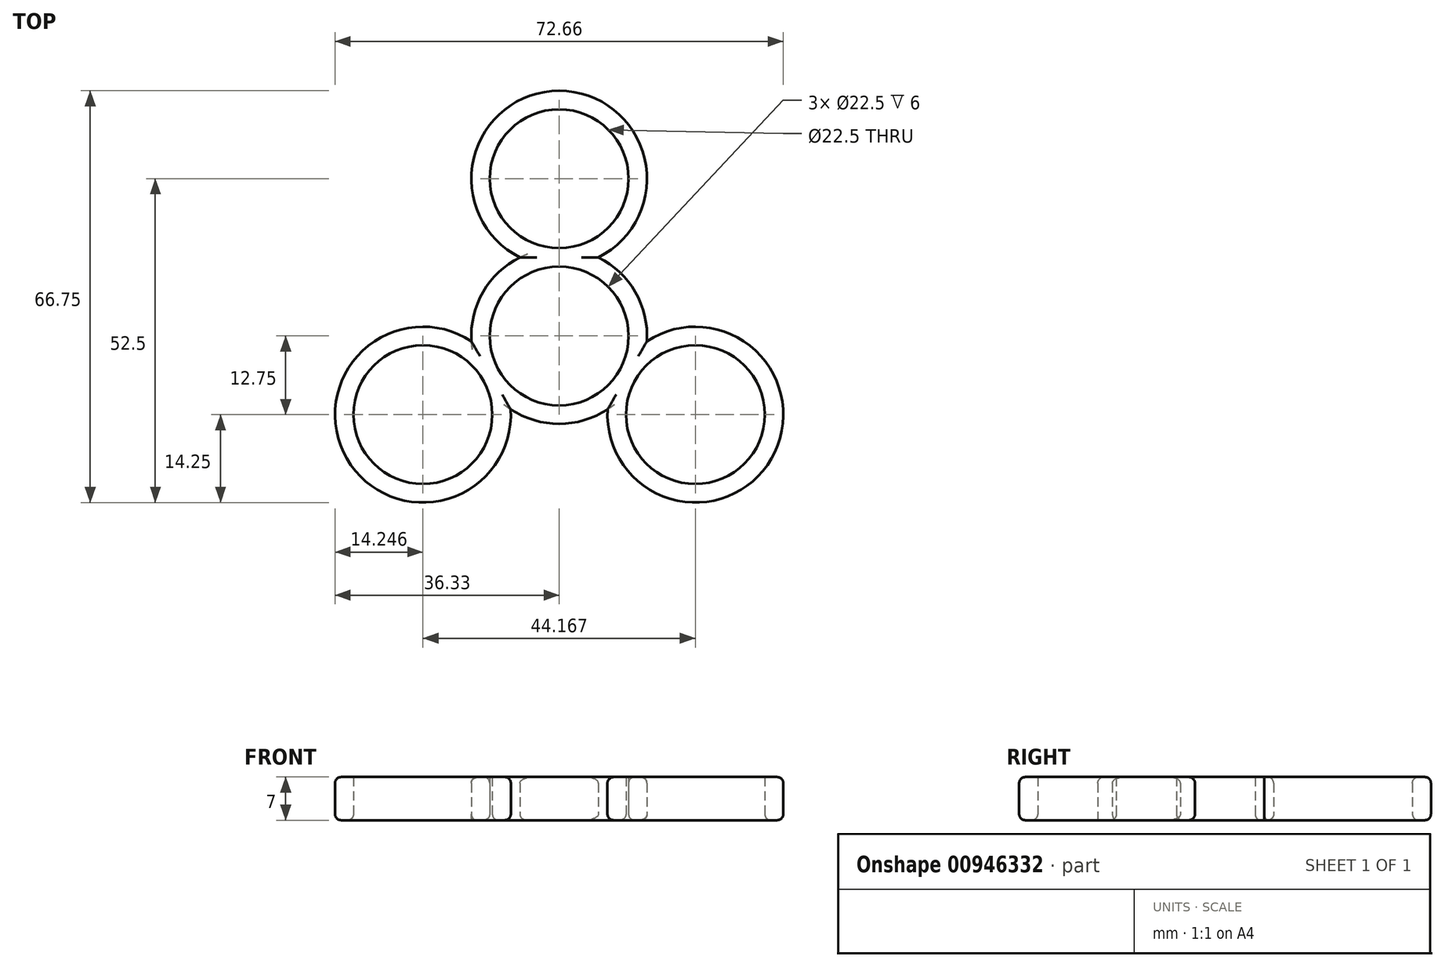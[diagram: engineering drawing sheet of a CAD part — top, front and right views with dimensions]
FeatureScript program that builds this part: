
annotation { "Feature Type Name" : "Feature", "Feature Type Description" : "" }
export const myFeature = defineFeature(function(context is Context, id is Id, definition is map)
    precondition{}
    {
        {
            var Q0;
            Q0=qCreatedBy(makeId("Top.planeOp"),FACE);
            var sketch = newSketch(context, id + "F0", { "sketchPlane" : qUnion([Q0])});
            skArc(sketch, "E0", {"start": v(9.74, 5.62) * mm, "mid": v(0, 11.25) * mm, "end": v(-9.74, 5.62) * mm});
            skCircle(sketch, "E1", {"center": v(0, 25.5) * mm, "radius": 11.25 * mm});
            skArc(sketch, "E2", {"start": v(-6.36, 12.75) * mm, "mid": v(-9.77, 10.38) * mm, "end": v(-12.34, 7.12) * mm});
            skArc(sketch, "E3", {"start": v(6.36, 12.75) * mm, "mid": v(0, 39.75) * mm, "end": v(-6.36, 12.75) * mm});
            skArc(sketch, "E4.trimOffspring", {"start": v(12.34, 7.12) * mm, "mid": v(9.77, 10.38) * mm, "end": v(6.36, 12.75) * mm});
            skArc(sketch, "E5.1.0", {"start": v(-14.22, -0.86) * mm, "mid": v(-34.42, -19.87) * mm, "end": v(-7.86, -11.89) * mm});
            skCircle(sketch, "E5.1.1", {"center": v(-22.08, -12.75) * mm, "radius": 11.25 * mm});
            skArc(sketch, "E5.1.2", {"start": v(-7.86, -11.89) * mm, "mid": v(-4.1, -13.65) * mm, "end": v(0, -14.25) * mm});
            skArc(sketch, "E5.1.3", {"start": v(-9.74, 5.63) * mm, "mid": v(-9.74, -5.62) * mm, "end": v(0, -11.25) * mm});
            skArc(sketch, "E5.1.4", {"start": v(-12.34, 7.13) * mm, "mid": v(-13.87, 3.27) * mm, "end": v(-14.22, -0.86) * mm});
            skArc(sketch, "E5.2.0", {"start": v(7.86, -11.89) * mm, "mid": v(34.42, -19.88) * mm, "end": v(14.22, -0.86) * mm});
            skCircle(sketch, "E5.2.1", {"center": v(22.08, -12.75) * mm, "radius": 11.25 * mm});
            skArc(sketch, "E5.2.2", {"start": v(14.22, -0.86) * mm, "mid": v(13.87, 3.27) * mm, "end": v(12.34, 7.12) * mm});
            skArc(sketch, "E5.2.3", {"start": v(0, -11.25) * mm, "mid": v(9.74, -5.63) * mm, "end": v(9.74, 5.62) * mm});
            skArc(sketch, "E5.2.4", {"start": v(0, -14.25) * mm, "mid": v(4.1, -13.65) * mm, "end": v(7.86, -11.89) * mm});
            skLineSegment(sketch, "E6", {"start": v(4.42, 25.5) * mm, "end": v(-4.48, 25.5) * mm});
            skLineSegment(sketch, "E7", {"start": v(0, 21.78) * mm, "end": v(0, 30.17) * mm});
            skLineSegment(sketch, "E8", {"start": v(0, 4.75) * mm, "end": v(0, -5.57) * mm});
            skLineSegment(sketch, "E9", {"start": v(3.64, 0) * mm, "end": v(-3.58, 0) * mm});
            skLineSegment(sketch, "E10", {"start": v(22.08, -8.41) * mm, "end": v(22.08, -18.09) * mm});
            skLineSegment(sketch, "E11", {"start": v(17.58, -12.75) * mm, "end": v(27.39, -12.75) * mm});
            skLineSegment(sketch, "E12", {"start": v(-22.08, -9.06) * mm, "end": v(-22.08, -17.31) * mm});
            skLineSegment(sketch, "E13", {"start": v(-26.94, -12.75) * mm, "end": v(-17, -12.75) * mm});
            skSolve(sketch);
        }
        {
            var Q0;
            Q0 = qSketchRegion(id + "F0", true);
            extrude(context, id + "F1", {"entities" : qUnion([Q0]), "depth" : 7 * mm, "offsetDistance" : 25 * mm});
        }
        {
            var Q0;
            Q0=makeQuery(id+"F1.opExtrude","CAP_EDGE",EDGE,{"disambiguationData":[OSD([sQuery(id+"F0.wireOp",EDGE,"E3")])],"isStart":false});
            var Q1;
            Q1=makeQuery(id+"F1.opExtrude","CAP_EDGE",EDGE,{"disambiguationData":[OSD([sQuery(id+"F0.wireOp",EDGE,"E5.2.0")])],"isStart":false});
            var Q2;
            Q2=makeQuery(id+"F1.opExtrude","CAP_EDGE",EDGE,{"disambiguationData":[OSD([sQuery(id+"F0.wireOp",EDGE,"E5.1.0")])],"isStart":false});
            var Q3;
            Q3=makeQuery(id+"F1.opExtrude","CAP_EDGE",EDGE,{"disambiguationData":[OSD([sQuery(id+"F0.wireOp",EDGE,"E2"),sQuery(id+"F0.wireOp",EDGE,"E5.1.4")])],"isStart":false});
            var Q4;
            Q4=makeQuery(id+"F1.opExtrude","CAP_EDGE",EDGE,{"disambiguationData":[OSD([sQuery(id+"F0.wireOp",EDGE,"E5.1.2"),sQuery(id+"F0.wireOp",EDGE,"E5.2.4")])],"isStart":false});
            var Q5;
            Q5=makeQuery(id+"F1.opExtrude","CAP_EDGE",EDGE,{"disambiguationData":[OSD([sQuery(id+"F0.wireOp",EDGE,"E4.trimOffspring"),sQuery(id+"F0.wireOp",EDGE,"E5.2.2")])],"isStart":true});
            var Q6;
            Q6=makeQuery(id+"F1.opExtrude","CAP_EDGE",EDGE,{"disambiguationData":[OSD([sQuery(id+"F0.wireOp",EDGE,"E5.2.0")])],"isStart":true});
            var Q7;
            Q7=makeQuery(id+"F1.opExtrude","CAP_EDGE",EDGE,{"disambiguationData":[OSD([sQuery(id+"F0.wireOp",EDGE,"E5.2.1")])],"isStart":true});
            var Q8;
            Q8=makeQuery(id+"F1.opExtrude","CAP_EDGE",EDGE,{"disambiguationData":[OSD([sQuery(id+"F0.wireOp",EDGE,"E0"),sQuery(id+"F0.wireOp",EDGE,"E5.1.3"),sQuery(id+"F0.wireOp",EDGE,"E5.2.3")])],"isStart":true});
            var Q9;
            Q9=makeQuery(id+"F1.opExtrude","CAP_EDGE",EDGE,{"disambiguationData":[OSD([sQuery(id+"F0.wireOp",EDGE,"E5.1.1")])],"isStart":true});
            var Q10;
            Q10=makeQuery(id+"F1.opExtrude","CAP_EDGE",EDGE,{"disambiguationData":[OSD([sQuery(id+"F0.wireOp",EDGE,"E5.1.0")])],"isStart":true});
            var Q11;
            Q11=makeQuery(id+"F1.opExtrude","CAP_EDGE",EDGE,{"disambiguationData":[OSD([sQuery(id+"F0.wireOp",EDGE,"E3")])],"isStart":true});
            var Q12;
            Q12=makeQuery(id+"F1.opExtrude","CAP_EDGE",EDGE,{"disambiguationData":[OSD([sQuery(id+"F0.wireOp",EDGE,"E1")])],"isStart":true});
            var Q13;
            Q13=makeQuery(id+"F1.opExtrude","CAP_EDGE",EDGE,{"disambiguationData":[OSD([sQuery(id+"F0.wireOp",EDGE,"E1")])],"isStart":false});
            fillet(context, id + "F2", {"entities" : qUnion([Q0, Q1, Q2, Q3, Q4, Q5, Q6, Q7, Q8, Q9, Q10, Q11, Q12, Q13]), "tangentPropagation" : true, "radius" : 1 * mm, "defaultsChanged" : false, "vertexSettings" : [], "allowEdgeOverflow" : false});
        }
        {
            var Q0;
            Q0=makeQuery(id+"F1.opExtrude","CAP_EDGE",EDGE,{"disambiguationData":[OSD([sQuery(id+"F0.wireOp",EDGE,"E4.trimOffspring"),sQuery(id+"F0.wireOp",EDGE,"E5.2.2")])],"isStart":false});
            fillet(context, id + "F3", {"entities" : qUnion([Q0]), "tangentPropagation" : true, "radius" : 1 * mm, "defaultsChanged" : true, "vertexSettings" : [], "allowEdgeOverflow" : false});
        }
    });
